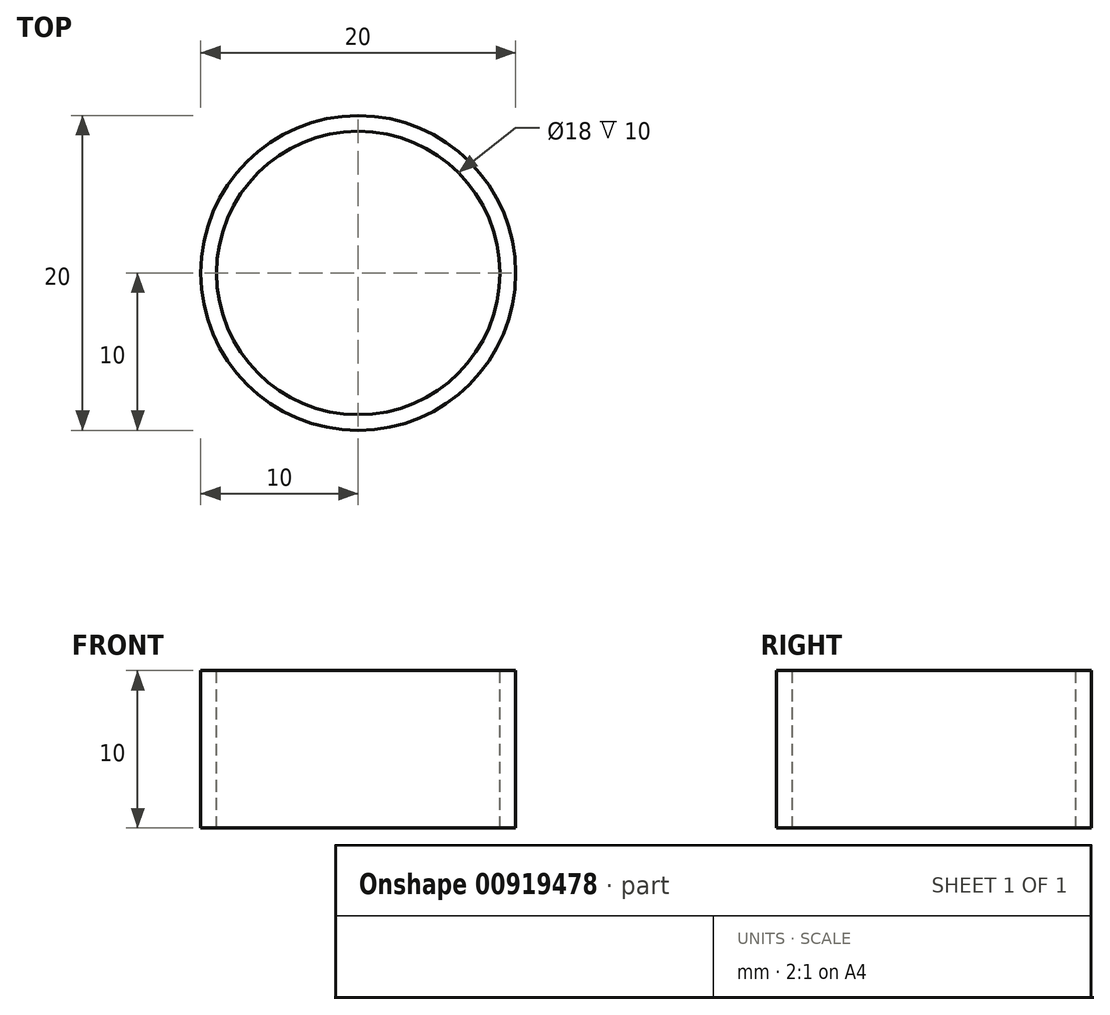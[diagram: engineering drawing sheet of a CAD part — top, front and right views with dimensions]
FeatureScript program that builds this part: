
annotation { "Feature Type Name" : "Feature", "Feature Type Description" : "" }
export const myFeature = defineFeature(function(context is Context, id is Id, definition is map)
    precondition{}
    {
        {
            var Q0;
            Q0=qCreatedBy(makeId("Top.planeOp"),FACE);
            var sketch = newSketch(context, id + "F0", { "sketchPlane" : qUnion([Q0])});
            skCircle(sketch, "E0", {"center": v(0, 0) * mm, "radius": 10 * mm});
            skSolve(sketch);
        }
        {
            var Q0;
            Q0=qSketchRegion(id+"F0",true);
            extrude(context, id + "F1", {"entities" : qUnion([Q0]), "depth" : 10 * mm, "offsetDistance" : 25 * mm, "symmetric" : true});
        }
        {
            var Q0;
            Q0=makeQuery(id+"F1.opExtrude","CAP_FACE",FACE,{"disambiguationData":[OSD([sQuery(id+"F0.wireOp",EDGE,"E0")])],"isStart":false});
            var sketch = newSketch(context, id + "F2", { "sketchPlane" : qUnion([Q0])});
            skCircle(sketch, "E1", {"center": v(0, 0) * mm, "radius": 9 * mm});
            skSolve(sketch);
        }
        {
            var Q0;
            Q0 = qSketchRegion(id + "F2", true);
            extrude(context, id + "F3", {"entities" : qUnion([Q0]), "operationType" : NewBodyOperationType.REMOVE, "endBound" : BoundingType.UP_TO_NEXT, "oppositeDirection" : true, "depth" : 25 * mm, "offsetDistance" : 25 * mm});
        }
    });
